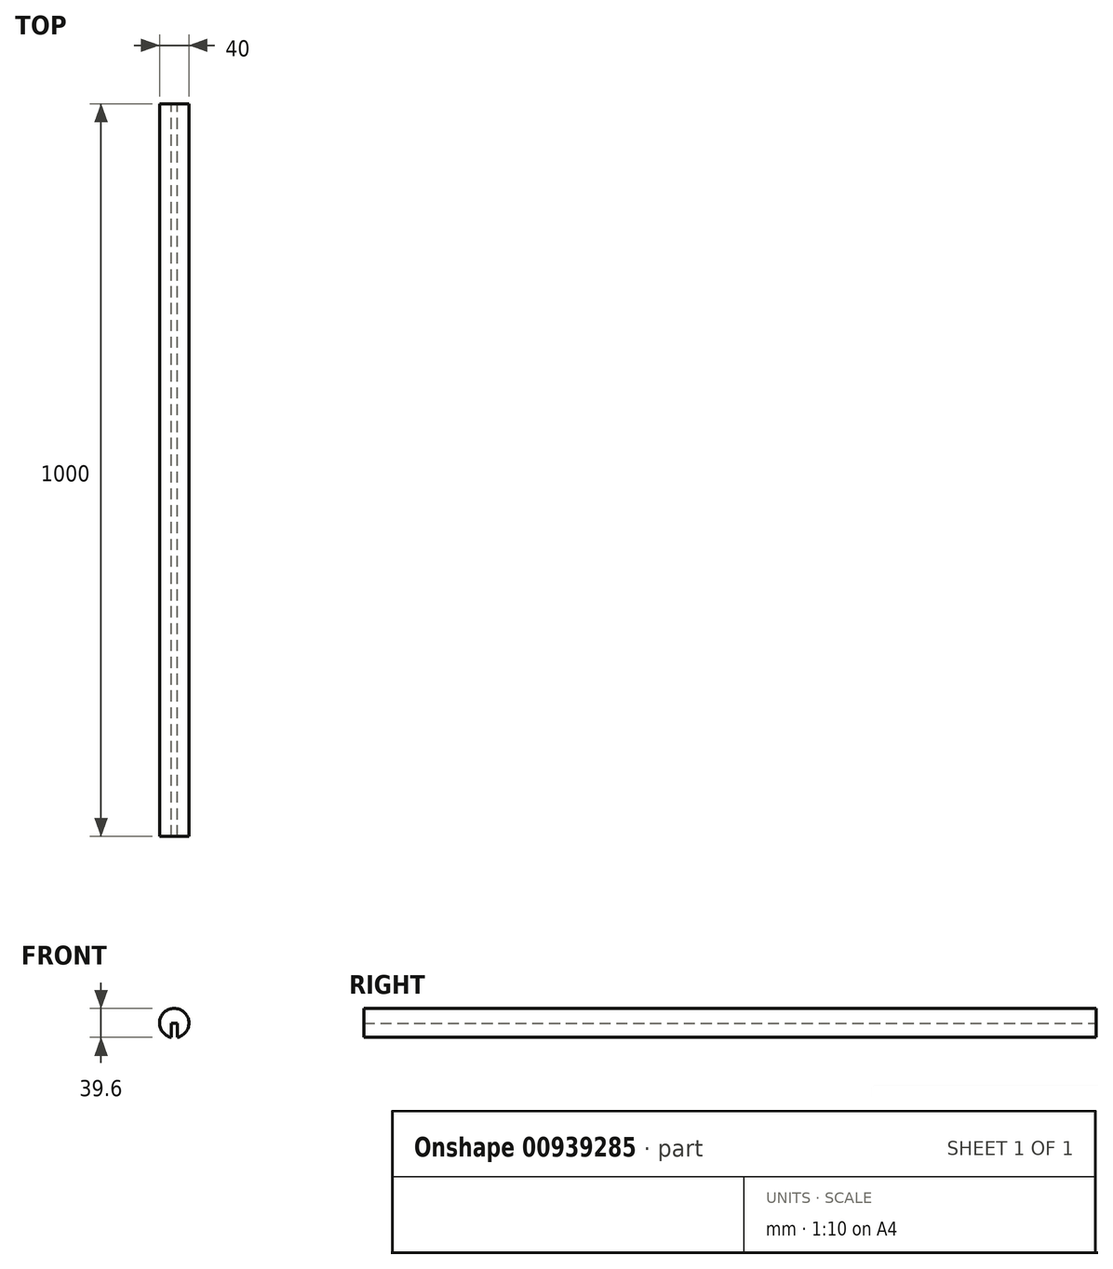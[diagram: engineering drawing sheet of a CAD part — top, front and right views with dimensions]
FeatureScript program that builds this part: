
annotation { "Feature Type Name" : "Feature", "Feature Type Description" : "" }
export const myFeature = defineFeature(function(context is Context, id is Id, definition is map)
    precondition{}
    {
        {
            var Q0;
            Q0=qCreatedBy(makeId("Front.planeOp"),FACE);
            var sketch = newSketch(context, id + "F0", { "sketchPlane" : qUnion([Q0])});
            skArc(sketch, "E0", {"start": v(4, -19.6) * mm, "mid": v(0, 20) * mm, "end": v(-4, -19.6) * mm});
            skLineSegment(sketch, "E1.top", {"start": v(-4, -0.6) * mm, "end": v(4, -0.6) * mm});
            skLineSegment(sketch, "E1.left", {"start": v(-4, -19.6) * mm, "end": v(-4, -0.6) * mm});
            skLineSegment(sketch, "E1.right", {"start": v(4, -19.6) * mm, "end": v(4, -0.6) * mm});
            skSolve(sketch);
        }
        {
            var Q0;
            Q0=makeQuery(id+"F0.imprint","IMPRINT",FACE,{"disambiguationData":[TD([[makeQuery(id+"F0.imprint","IMPRINT",EDGE,{"derivedFrom":sQuery(id+"F0.wireOp",EDGE,"E0")}),1.0]])]});
            extrude(context, id + "F1", {"entities" : qUnion([Q0]), "depth" : 1000 * mm, "offsetDistance" : 25 * mm});
        }
    });
